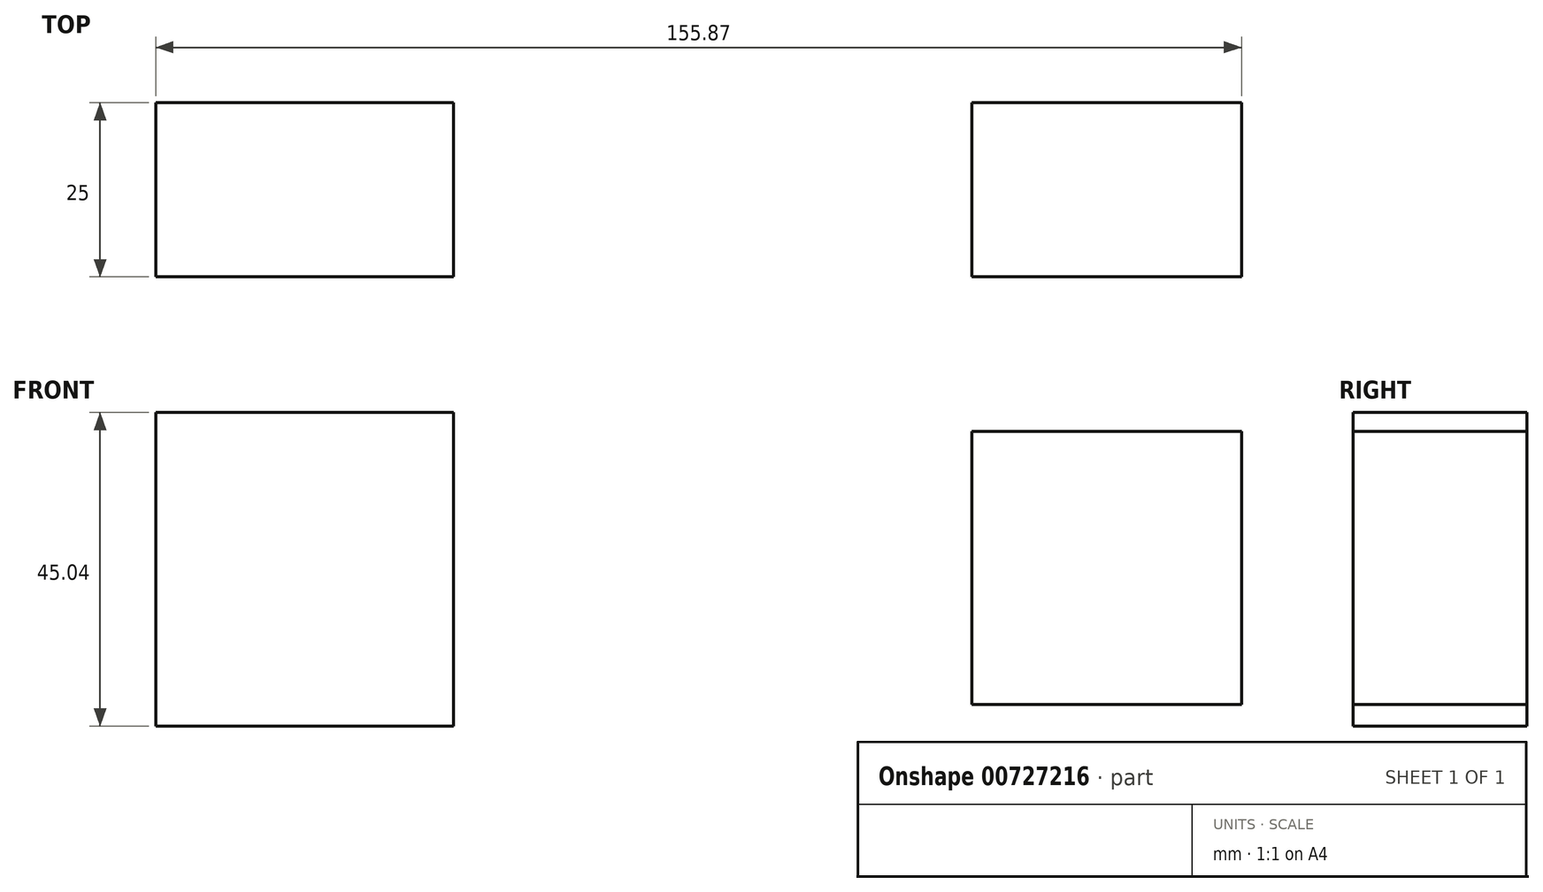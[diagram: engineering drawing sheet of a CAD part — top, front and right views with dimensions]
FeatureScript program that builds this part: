
annotation { "Feature Type Name" : "Feature", "Feature Type Description" : "" }
export const myFeature = defineFeature(function(context is Context, id is Id, definition is map)
    precondition{}
    {
        {
            var Q0;
            Q0=qCreatedBy(makeId("Front.planeOp"),FACE);
            var sketch = newSketch(context, id + "F0", { "sketchPlane" : qUnion([Q0])});
            skLineSegment(sketch, "E0.bottom", {"start": v(-106.64, 7.77) * mm, "end": v(-63.92, 7.77) * mm});
            skLineSegment(sketch, "E0.top", {"start": v(-106.64, 52.81) * mm, "end": v(-63.92, 52.81) * mm});
            skLineSegment(sketch, "E0.left", {"start": v(-106.64, 7.77) * mm, "end": v(-106.64, 52.81) * mm});
            skLineSegment(sketch, "E0.right", {"start": v(-63.92, 7.77) * mm, "end": v(-63.92, 52.81) * mm});
            skPoint(sketch, "E0.middle", {"position": v(-85.28, 30.29) * mm});
            skLineSegment(sketch, "E1.bottom", {"start": v(10.51, 10.88) * mm, "end": v(49.23, 10.88) * mm});
            skLineSegment(sketch, "E1.top", {"start": v(10.51, 50.1) * mm, "end": v(49.23, 50.1) * mm});
            skLineSegment(sketch, "E1.left", {"start": v(10.51, 10.88) * mm, "end": v(10.51, 50.1) * mm});
            skLineSegment(sketch, "E1.right", {"start": v(49.23, 10.88) * mm, "end": v(49.23, 50.1) * mm});
            skPoint(sketch, "E1.middle", {"position": v(29.87, 30.49) * mm});
            skSolve(sketch);
        }
        {
            var Q0;
            Q0=makeQuery(id+"F0.imprint","IMPRINT",FACE,{"disambiguationData":[TD([[makeQuery(id+"F0.imprint","IMPRINT",EDGE,{"derivedFrom":sQuery(id+"F0.wireOp",EDGE,"E1.bottom")}),1.0]])]});
            var Q1;
            Q1=makeQuery(id+"F0.imprint","IMPRINT",FACE,{"disambiguationData":[TD([[makeQuery(id+"F0.imprint","IMPRINT",EDGE,{"derivedFrom":sQuery(id+"F0.wireOp",EDGE,"E0.bottom")}),1.0]])]});
            extrude(context, id + "F1", {"entities" : qUnion([Q0, Q1]), "depth" : 25 * mm, "offsetDistance" : 25 * mm});
        }
    });
